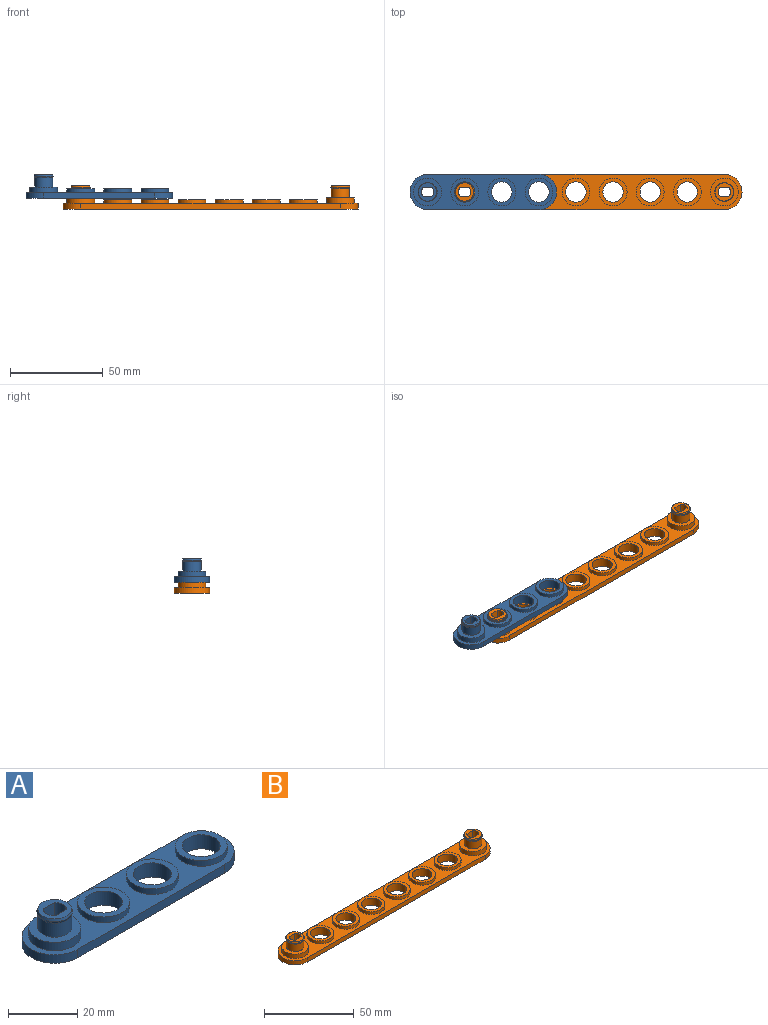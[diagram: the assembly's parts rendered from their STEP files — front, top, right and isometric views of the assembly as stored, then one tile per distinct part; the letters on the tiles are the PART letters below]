
ASSEMBLY  parts=2 mates=1
PART A: 25 faces, bbox 79x19x12.5 mm
  f0: cylinder r=9.5mm len=19mm, axis (0,0,-1), area 89.5mm2, adj f1,f5,f7,f8
  f1: plane 60x3mm, normal (0,1,0), area 180mm2, adj f0,f2,f7,f8
  f2: cylinder r=9.5mm len=19mm, axis (0,0,-1), area 89.5mm2, adj f1,f5,f7,f8
  f3: cylinder r=5.5mm len=11mm, axis (0,0,-1), area 172.8mm2, adj f8,f13
  f4: cylinder r=5.5mm len=11mm, axis (0,0,-1), area 172.8mm2, adj f8,f11
  f5: plane 60x3mm, normal (0,-1,0), area 180mm2, adj f0,f2,f7,f8
  f6: cylinder r=5.5mm len=11mm, axis (0,0,-1), area 172.8mm2, adj f8,f15
  f7: plane 79x19mm, normal (0,0,1), area 716.7mm2, adj f0,f1,f2,f5,f9,f10,f12,f14
  f8: plane 79x19mm, normal (0,0,-1), area 1108.8mm2, adj f0,f1,f2,f3,f4,f5,f6,f17
  f9: cylinder r=7.5mm len=15mm, axis (0,0,-1), area 141.4mm2, adj f7,f21
  f10: cylinder r=7.5mm len=15mm, axis (0,0,-1), area 94.2mm2, adj f7,f11
  f11: plane 15x15mm, normal (0,0,1), area 81.7mm2, adj f4,f10
  f12: cylinder r=7.5mm len=15mm, axis (0,0,-1), area 94.2mm2, adj f7,f13
  f13: plane 15x15mm, normal (0,0,1), area 81.7mm2, adj f3,f12
  f14: cylinder r=7.5mm len=15mm, axis (0,0,-1), area 94.2mm2, adj f7,f15
  f15: plane 15x15mm, normal (0,0,1), area 81.7mm2, adj f6,f14
  f16: cylinder r=4.9mm len=9.8mm, axis (0,0,-1), area 153.9mm2, adj f21,f23
  f17: cylinder r=3.35mm len=12.5mm, axis (0,0,-1), area 68.7mm2, adj f8,f18,f20,f22
  f18: plane 12.5x4.57mm, normal (0,-1,0), area 57.1mm2, adj f8,f17,f19,f22
  f19: cylinder r=3.35mm len=12.5mm, axis (0,0,-1), area 68.7mm2, adj f8,f18,f20,f22
  f20: plane 12.5x4.57mm, normal (0,1,0), area 57.1mm2, adj f8,f17,f19,f22
  f21: plane 15x15mm, normal (0,0,1), area 101.3mm2, adj f9,f16
  f22: plane 9.8x9.8mm, normal (0,0,1), area 45.8mm2, adj f17,f18,f19,f20,f24
  f23: cone r=5.15mm half-angle=18.4deg, axis (0,0,1), area 25mm2, adj f16,f24
  f24: cone r=4.9mm half-angle=18.4deg, axis (0,0,-1), area 25mm2, adj f22,f23
PART B: 44 faces, bbox 159x19x12.5 mm
  f0: cylinder r=9.5mm len=19mm, axis (0,0,-1), area 89.5mm2, adj f1,f9,f10,f11
  f1: plane 140x3mm, normal (0,1,0), area 420mm2, adj f0,f2,f10,f11
  f2: cylinder r=9.5mm len=19mm, axis (0,0,-1), area 89.5mm2, adj f1,f9,f10,f11
  f3: cylinder r=5.5mm len=11mm, axis (0,0,-1), area 172.8mm2, adj f11,f24
  f4: cylinder r=5.5mm len=11mm, axis (0,0,-1), area 172.8mm2, adj f11,f22
  f5: cylinder r=5.5mm len=11mm, axis (0,0,-1), area 172.8mm2, adj f11,f20
  f6: cylinder r=5.5mm len=11mm, axis (0,0,-1), area 172.8mm2, adj f11,f18
  f7: cylinder r=5.5mm len=11mm, axis (0,0,-1), area 172.8mm2, adj f11,f16
  f8: cylinder r=5.5mm len=11mm, axis (0,0,-1), area 172.8mm2, adj f11,f14
  f9: plane 140x3mm, normal (0,-1,0), area 420mm2, adj f0,f2,f10,f11
  f10: plane 159x19mm, normal (0,0,1), area 1529.8mm2, adj f0,f1,f2,f9,f12,f13,f15,f17
  f11: plane 159x19mm, normal (0,0,-1), area 2314.1mm2, adj f0,f1,f2,f3,f4,f5,f6,f7
  f12: cylinder r=7.5mm len=15mm, axis (0,0,-1), area 141.4mm2, adj f10,f31
  f13: cylinder r=7.5mm len=15mm, axis (0,0,-1), area 94.2mm2, adj f10,f14
  f14: plane 15x15mm, normal (0,0,1), area 81.7mm2, adj f8,f13
  f15: cylinder r=7.5mm len=15mm, axis (0,0,-1), area 94.2mm2, adj f10,f16
  f16: plane 15x15mm, normal (0,0,1), area 81.7mm2, adj f7,f15
  f17: cylinder r=7.5mm len=15mm, axis (0,0,-1), area 94.2mm2, adj f10,f18
  f18: plane 15x15mm, normal (0,0,1), area 81.7mm2, adj f6,f17
  f19: cylinder r=7.5mm len=15mm, axis (0,0,-1), area 94.2mm2, adj f10,f20
  f20: plane 15x15mm, normal (0,0,1), area 81.7mm2, adj f5,f19
  f21: cylinder r=7.5mm len=15mm, axis (0,0,-1), area 94.2mm2, adj f10,f22
  f22: plane 15x15mm, normal (0,0,1), area 81.7mm2, adj f4,f21
  f23: cylinder r=7.5mm len=15mm, axis (0,0,-1), area 94.2mm2, adj f10,f24
  f24: plane 15x15mm, normal (0,0,1), area 81.7mm2, adj f3,f23
  f25: cylinder r=7.5mm len=15mm, axis (0,0,-1), area 141.4mm2, adj f10,f40
  f26: cylinder r=4.9mm len=9.8mm, axis (0,0,-1), area 153.9mm2, adj f31,f33
  f27: cylinder r=3.35mm len=12.5mm, axis (0,0,-1), area 68.7mm2, adj f11,f28,f30,f32
  f28: plane 12.5x4.57mm, normal (0,-1,0), area 57.1mm2, adj f11,f27,f29,f32
  f29: cylinder r=3.35mm len=12.5mm, axis (0,0,-1), area 68.7mm2, adj f11,f28,f30,f32
  f30: plane 12.5x4.57mm, normal (0,1,0), area 57.1mm2, adj f11,f27,f29,f32
  f31: plane 15x15mm, normal (0,0,1), area 101.3mm2, adj f12,f26
  f32: plane 9.8x9.8mm, normal (0,0,1), area 45.8mm2, adj f27,f28,f29,f30,f34
  f33: cone r=5.15mm half-angle=18.4deg, axis (0,0,1), area 25mm2, adj f26,f34
  f34: cone r=4.9mm half-angle=18.4deg, axis (0,0,-1), area 25mm2, adj f32,f33
  f35: cylinder r=4.9mm len=9.8mm, axis (0,0,-1), area 153.9mm2, adj f40,f42
  f36: cylinder r=3.35mm len=12.5mm, axis (0,0,-1), area 68.7mm2, adj f11,f37,f39,f41
  f37: plane 12.5x4.57mm, normal (0,-1,0), area 57.1mm2, adj f11,f36,f38,f41
  f38: cylinder r=3.35mm len=12.5mm, axis (0,0,-1), area 68.7mm2, adj f11,f37,f39,f41
  f39: plane 12.5x4.57mm, normal (0,1,0), area 57.1mm2, adj f11,f36,f38,f41
  f40: plane 15x15mm, normal (0,0,1), area 101.3mm2, adj f25,f35
  f41: plane 9.8x9.8mm, normal (0,0,1), area 45.8mm2, adj f36,f37,f38,f39,f43
  f42: cone r=5.15mm half-angle=18.4deg, axis (0,0,1), area 25mm2, adj f35,f43
  f43: cone r=4.9mm half-angle=18.4deg, axis (0,0,-1), area 25mm2, adj f41,f42
PLACE A t=(68.39,74.98,29.28)mm
PLACE B t=(88.39,74.98,23.4)mm
MATE cylindrical B.f26 <-> A.f4  axis (0,0,1) through (88.39,74.98,29.4)mm
